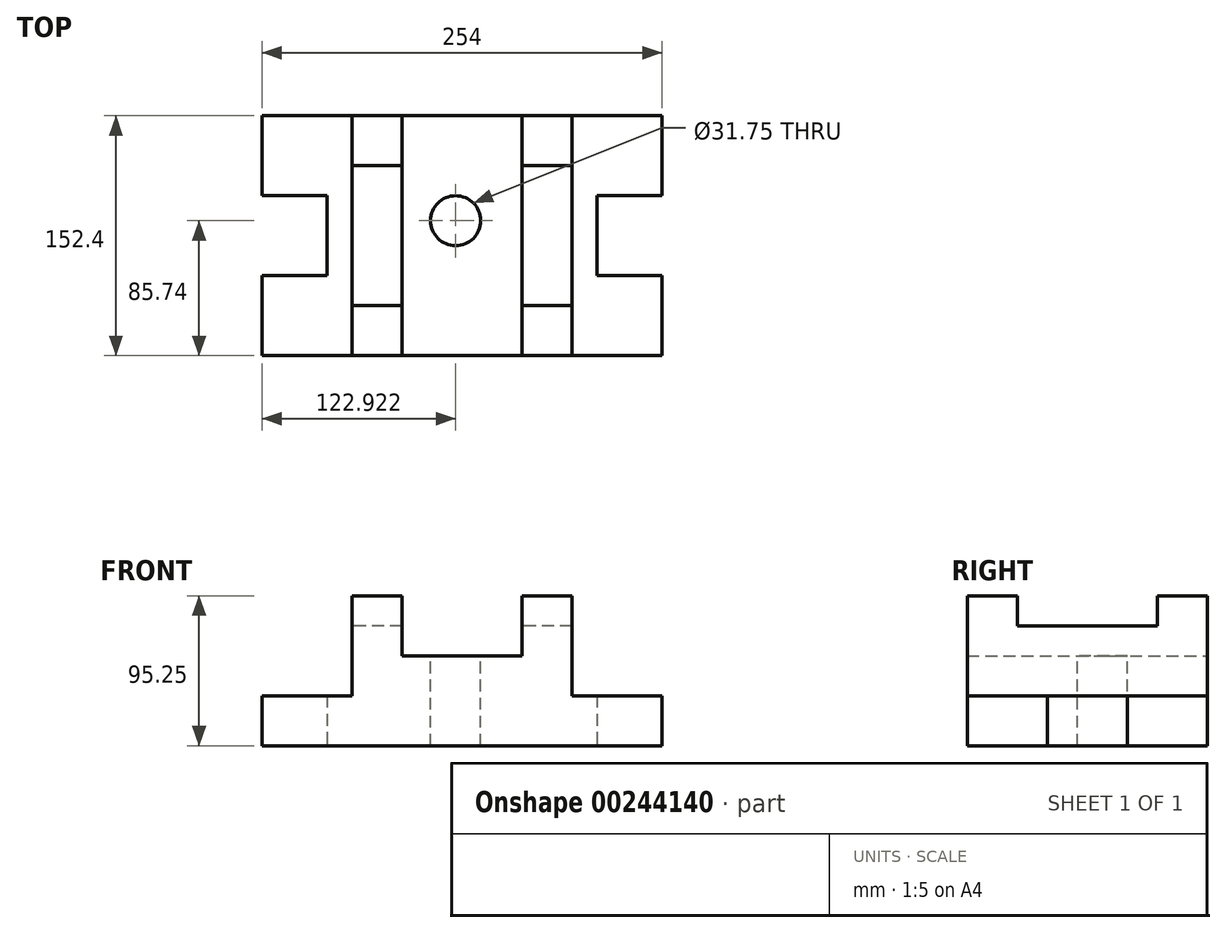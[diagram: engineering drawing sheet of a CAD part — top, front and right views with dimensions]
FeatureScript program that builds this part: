
annotation { "Feature Type Name" : "Feature", "Feature Type Description" : "" }
export const myFeature = defineFeature(function(context is Context, id is Id, definition is map)
    precondition{}
    {
        {
            var Q0;
            Q0=qCreatedBy(makeId("Top.planeOp"),FACE);
            var sketch = newSketch(context, id + "F0", { "sketchPlane" : qUnion([Q0])});
            skLineSegment(sketch, "E0.bottom", {"start": v(-99.04, 50.8) * mm, "end": v(154.96, 50.8) * mm});
            skLineSegment(sketch, "E0.top", {"start": v(-99.04, -101.6) * mm, "end": v(154.96, -101.6) * mm});
            skLineSegment(sketch, "E0.left", {"start": v(-99.04, 50.8) * mm, "end": v(-99.04, -101.6) * mm});
            skLineSegment(sketch, "E0.right", {"start": v(154.96, 50.8) * mm, "end": v(154.96, -101.6) * mm});
            skLineSegment(sketch, "E1", {"start": v(-99.04, 50.8) * mm, "end": v(-99.04, 0) * mm});
            skLineSegment(sketch, "E2.bottom", {"start": v(-99.04, 0) * mm, "end": v(-57.76, 0) * mm});
            skLineSegment(sketch, "E2.top", {"start": v(-99.04, -50.8) * mm, "end": v(-57.76, -50.8) * mm});
            skLineSegment(sketch, "E2.left", {"start": v(-99.04, 0) * mm, "end": v(-99.04, -50.8) * mm});
            skLineSegment(sketch, "E2.right", {"start": v(-57.76, 0) * mm, "end": v(-57.76, -50.8) * mm});
            skLineSegment(sketch, "E3.bottom", {"start": v(154.96, 0) * mm, "end": v(113.69, 0) * mm});
            skLineSegment(sketch, "E3.top", {"start": v(154.96, -50.8) * mm, "end": v(113.69, -50.8) * mm});
            skLineSegment(sketch, "E3.left", {"start": v(154.96, 0) * mm, "end": v(154.96, -50.8) * mm});
            skLineSegment(sketch, "E3.right", {"start": v(113.69, 0) * mm, "end": v(113.69, -50.8) * mm});
            skSolve(sketch);
        }
        {
            var Q0;
            Q0=makeQuery(id+"F0.imprint","IMPRINT",FACE,{"disambiguationData":[TD([[makeQuery(id+"F0.imprint","IMPRINT",EDGE,{"derivedFrom":sQuery(id+"F0.wireOp",EDGE,"E0.bottom")}),-1.0]])]});
            extrude(context, id + "F1", {"entities" : qUnion([Q0]), "depth" : 31.75 * mm});
        }
        {
            var Q0;
            Q0=makeQuery(id+"F1.opExtrude","CAP_FACE",FACE,{"disambiguationData":[OSD([sQuery(id+"F0.wireOp",EDGE,"E0.bottom"),sQuery(id+"F0.wireOp",EDGE,"E0.top"),sQuery(id+"F0.wireOp",EDGE,"E0.left"),sQuery(id+"F0.wireOp",EDGE,"E0.right"),sQuery(id+"F0.wireOp",EDGE,"E1"),sQuery(id+"F0.wireOp",EDGE,"E2.bottom"),sQuery(id+"F0.wireOp",EDGE,"E2.top"),sQuery(id+"F0.wireOp",EDGE,"E2.right"),sQuery(id+"F0.wireOp",EDGE,"E3.bottom"),sQuery(id+"F0.wireOp",EDGE,"E3.top"),sQuery(id+"F0.wireOp",EDGE,"E3.right")])],"isStart":false});
            var sketch = newSketch(context, id + "F2", { "sketchPlane" : qUnion([Q0])});
            skLineSegment(sketch, "E4.bottom", {"start": v(-41.89, 50.8) * mm, "end": v(97.81, 50.8) * mm});
            skLineSegment(sketch, "E4.top", {"start": v(-41.89, -101.6) * mm, "end": v(97.81, -101.6) * mm});
            skLineSegment(sketch, "E4.left", {"start": v(-41.89, 50.8) * mm, "end": v(-41.89, -101.6) * mm});
            skLineSegment(sketch, "E4.right", {"start": v(97.81, 50.8) * mm, "end": v(97.81, -101.6) * mm});
            skSolve(sketch);
        }
        {
            var Q0;
            Q0=makeQuery(id+"F2.imprint","IMPRINT",FACE,{"disambiguationData":[TD([[makeQuery(id+"F2.imprint","IMPRINT",EDGE,{"derivedFrom":sQuery(id+"F2.wireOp",EDGE,"E4.bottom")}),-1.0]])]});
            extrude(context, id + "F3", {"entities" : qUnion([Q0]), "operationType" : NewBodyOperationType.ADD, "depth" : 25.4 * mm});
        }
        {
            var Q0;
            Q0=makeQuery(id+"F3.opExtrude","CAP_FACE",FACE,{"disambiguationData":[OSD([sQuery(id+"F2.wireOp",EDGE,"E4.bottom"),sQuery(id+"F2.wireOp",EDGE,"E4.top"),sQuery(id+"F2.wireOp",EDGE,"E4.left"),sQuery(id+"F2.wireOp",EDGE,"E4.right")])],"isStart":false});
            var sketch = newSketch(context, id + "F4", { "sketchPlane" : qUnion([Q0])});
            skCircle(sketch, "E5", {"center": v(23.88, -15.86) * mm, "radius": 15.88 * mm});
            skSolve(sketch);
        }
        {
            var Q0;
            Q0=sQuery(id+"F4.wireOp",VERTEX,"E5.center");
            var Q1;
            Q1=makeQuery(id+"F1.opExtrude","SWEPT_BODY",BODY,{"disambiguationData":[OSD([sQuery(id+"F0.wireOp",EDGE,"E0.bottom"),sQuery(id+"F0.wireOp",EDGE,"E0.top"),sQuery(id+"F0.wireOp",EDGE,"E0.left"),sQuery(id+"F0.wireOp",EDGE,"E0.right"),sQuery(id+"F0.wireOp",EDGE,"E1"),sQuery(id+"F0.wireOp",EDGE,"E2.bottom"),sQuery(id+"F0.wireOp",EDGE,"E2.top"),sQuery(id+"F0.wireOp",EDGE,"E2.right"),sQuery(id+"F0.wireOp",EDGE,"E3.bottom"),sQuery(id+"F0.wireOp",EDGE,"E3.top"),sQuery(id+"F0.wireOp",EDGE,"E3.right")])]});
            hole(context, id + "F5", {"style" : HoleStyle.SIMPLE, "endStyle" : HoleEndStyle.THROUGH, "holeDiameter" : 31.75 * mm, "locations" : qUnion([Q0]), "scope" : qUnion([Q1]), "isTappedThrough" : true});
        }
        {
            var Q0;
            Q0=makeQuery(id+"F3.opExtrude","CAP_FACE",FACE,{"disambiguationData":[OSD([sQuery(id+"F2.wireOp",EDGE,"E4.bottom"),sQuery(id+"F2.wireOp",EDGE,"E4.top"),sQuery(id+"F2.wireOp",EDGE,"E4.left"),sQuery(id+"F2.wireOp",EDGE,"E4.right")])],"isStart":false});
            var sketch = newSketch(context, id + "F6", { "sketchPlane" : qUnion([Q0])});
            skLineSegment(sketch, "E6.bottom", {"start": v(-41.89, 50.8) * mm, "end": v(-10.14, 50.8) * mm});
            skLineSegment(sketch, "E6.top", {"start": v(-41.89, 19.05) * mm, "end": v(-10.14, 19.05) * mm});
            skLineSegment(sketch, "E6.left", {"start": v(-41.89, 50.8) * mm, "end": v(-41.89, 19.05) * mm});
            skLineSegment(sketch, "E6.right", {"start": v(-10.14, 50.8) * mm, "end": v(-10.14, 19.05) * mm});
            skLineSegment(sketch, "E7.bottom", {"start": v(97.81, -101.6) * mm, "end": v(66.06, -101.6) * mm});
            skLineSegment(sketch, "E7.top", {"start": v(97.81, -69.85) * mm, "end": v(66.06, -69.85) * mm});
            skLineSegment(sketch, "E7.left", {"start": v(97.81, -101.6) * mm, "end": v(97.81, -69.85) * mm});
            skLineSegment(sketch, "E7.right", {"start": v(66.06, -101.6) * mm, "end": v(66.06, -69.85) * mm});
            skLineSegment(sketch, "E8.bottom", {"start": v(-41.89, -101.6) * mm, "end": v(-10.14, -101.6) * mm});
            skLineSegment(sketch, "E8.top", {"start": v(-41.89, -69.85) * mm, "end": v(-10.14, -69.85) * mm});
            skLineSegment(sketch, "E8.left", {"start": v(-41.89, -101.6) * mm, "end": v(-41.89, -69.85) * mm});
            skLineSegment(sketch, "E8.right", {"start": v(-10.14, -101.6) * mm, "end": v(-10.14, -69.85) * mm});
            skLineSegment(sketch, "E9.bottom", {"start": v(97.81, 50.8) * mm, "end": v(66.06, 50.8) * mm});
            skLineSegment(sketch, "E9.top", {"start": v(97.81, 19.05) * mm, "end": v(66.06, 19.05) * mm});
            skLineSegment(sketch, "E9.left", {"start": v(97.81, 50.8) * mm, "end": v(97.81, 19.05) * mm});
            skLineSegment(sketch, "E9.right", {"start": v(66.06, 50.8) * mm, "end": v(66.06, 19.05) * mm});
            skLineSegment(sketch, "E10", {"start": v(-10.14, -69.85) * mm, "end": v(-10.14, 19.05) * mm});
            skLineSegment(sketch, "E11", {"start": v(66.06, 19.05) * mm, "end": v(66.06, -69.85) * mm});
            skSolve(sketch);
        }
        {
            var Q0;
            Q0 = qSketchRegion(id + "F6", true);
            var Q1;
            {var subQ0=sQuery(id+"F6.wireOp",EDGE,"E6.top");Q1=makeQuery(id+"F6.imprint","IMPRINT",FACE,{"disambiguationData":[TD([[makeQuery(id+"F6.imprint","IMPRINT",EDGE,{"derivedFrom":subQ0}),-1.0]])]});}
            var Q2;
            {var subQ0=sQuery(id+"F6.wireOp",EDGE,"E7.top");Q2=makeQuery(id+"F6.imprint","IMPRINT",FACE,{"disambiguationData":[TD([[makeQuery(id+"F6.imprint","IMPRINT",EDGE,{"derivedFrom":subQ0}),-1.0]])]});}
            extrude(context, id + "F7", {"entities" : qUnion([Q0, Q1, Q2]), "operationType" : NewBodyOperationType.ADD, "depth" : 19.05 * mm});
        }
        {
            var Q0;
            Q0=makeQuery(id+"F7.opExtrude","CAP_FACE",FACE,{"disambiguationData":[OSD([sQuery(id+"F2.wireOp",EDGE,"E4.left"),sQuery(id+"F6.wireOp",EDGE,"E6.bottom"),sQuery(id+"F6.wireOp",EDGE,"E6.left"),sQuery(id+"F6.wireOp",EDGE,"E6.right"),sQuery(id+"F6.wireOp",EDGE,"E8.bottom"),sQuery(id+"F6.wireOp",EDGE,"E8.left"),sQuery(id+"F6.wireOp",EDGE,"E8.right"),sQuery(id+"F6.wireOp",EDGE,"E10")])],"isStart":false});
            var sketch = newSketch(context, id + "F8", { "sketchPlane" : qUnion([Q0])});
            skLineSegment(sketch, "E12.bottom", {"start": v(-41.89, -101.6) * mm, "end": v(-10.14, -101.6) * mm});
            skLineSegment(sketch, "E12.top", {"start": v(-41.89, -69.85) * mm, "end": v(-10.14, -69.85) * mm});
            skLineSegment(sketch, "E12.left", {"start": v(-41.89, -101.6) * mm, "end": v(-41.89, -69.85) * mm});
            skLineSegment(sketch, "E12.right", {"start": v(-10.14, -101.6) * mm, "end": v(-10.14, -69.85) * mm});
            skLineSegment(sketch, "E13.bottom", {"start": v(-10.14, 50.8) * mm, "end": v(-41.89, 50.8) * mm});
            skLineSegment(sketch, "E13.top", {"start": v(-10.14, 19.05) * mm, "end": v(-41.89, 19.05) * mm});
            skLineSegment(sketch, "E13.left", {"start": v(-10.14, 50.8) * mm, "end": v(-10.14, 19.05) * mm});
            skLineSegment(sketch, "E13.right", {"start": v(-41.89, 50.8) * mm, "end": v(-41.89, 19.05) * mm});
            skSolve(sketch);
        }
        {
            var Q0;
            Q0 = qSketchRegion(id + "F8", true);
            extrude(context, id + "F9", {"entities" : qUnion([Q0]), "operationType" : NewBodyOperationType.ADD, "depth" : 19.05 * mm});
        }
        {
            var Q0;
            Q0=makeQuery(id+"F7.opExtrude","CAP_FACE",FACE,{"disambiguationData":[OSD([sQuery(id+"F2.wireOp",EDGE,"E4.right"),sQuery(id+"F6.wireOp",EDGE,"E7.bottom"),sQuery(id+"F6.wireOp",EDGE,"E7.left"),sQuery(id+"F6.wireOp",EDGE,"E7.right"),sQuery(id+"F6.wireOp",EDGE,"E9.bottom"),sQuery(id+"F6.wireOp",EDGE,"E9.left"),sQuery(id+"F6.wireOp",EDGE,"E9.right"),sQuery(id+"F6.wireOp",EDGE,"E11")])],"isStart":false});
            var sketch = newSketch(context, id + "F10", { "sketchPlane" : qUnion([Q0])});
            skLineSegment(sketch, "E14.bottom", {"start": v(66.06, -101.6) * mm, "end": v(97.81, -101.6) * mm});
            skLineSegment(sketch, "E14.top", {"start": v(66.06, -69.85) * mm, "end": v(97.81, -69.85) * mm});
            skLineSegment(sketch, "E14.left", {"start": v(66.06, -101.6) * mm, "end": v(66.06, -69.85) * mm});
            skLineSegment(sketch, "E14.right", {"start": v(97.81, -101.6) * mm, "end": v(97.81, -69.85) * mm});
            skLineSegment(sketch, "E15.bottom", {"start": v(97.81, 50.8) * mm, "end": v(66.06, 50.8) * mm});
            skLineSegment(sketch, "E15.top", {"start": v(97.81, 19.05) * mm, "end": v(66.06, 19.05) * mm});
            skLineSegment(sketch, "E15.left", {"start": v(97.81, 50.8) * mm, "end": v(97.81, 19.05) * mm});
            skLineSegment(sketch, "E15.right", {"start": v(66.06, 50.8) * mm, "end": v(66.06, 19.05) * mm});
            skSolve(sketch);
        }
        {
            var Q0;
            Q0 = qSketchRegion(id + "F10", true);
            extrude(context, id + "F11", {"entities" : qUnion([Q0]), "operationType" : NewBodyOperationType.ADD, "depth" : 19.05 * mm});
        }
    });
